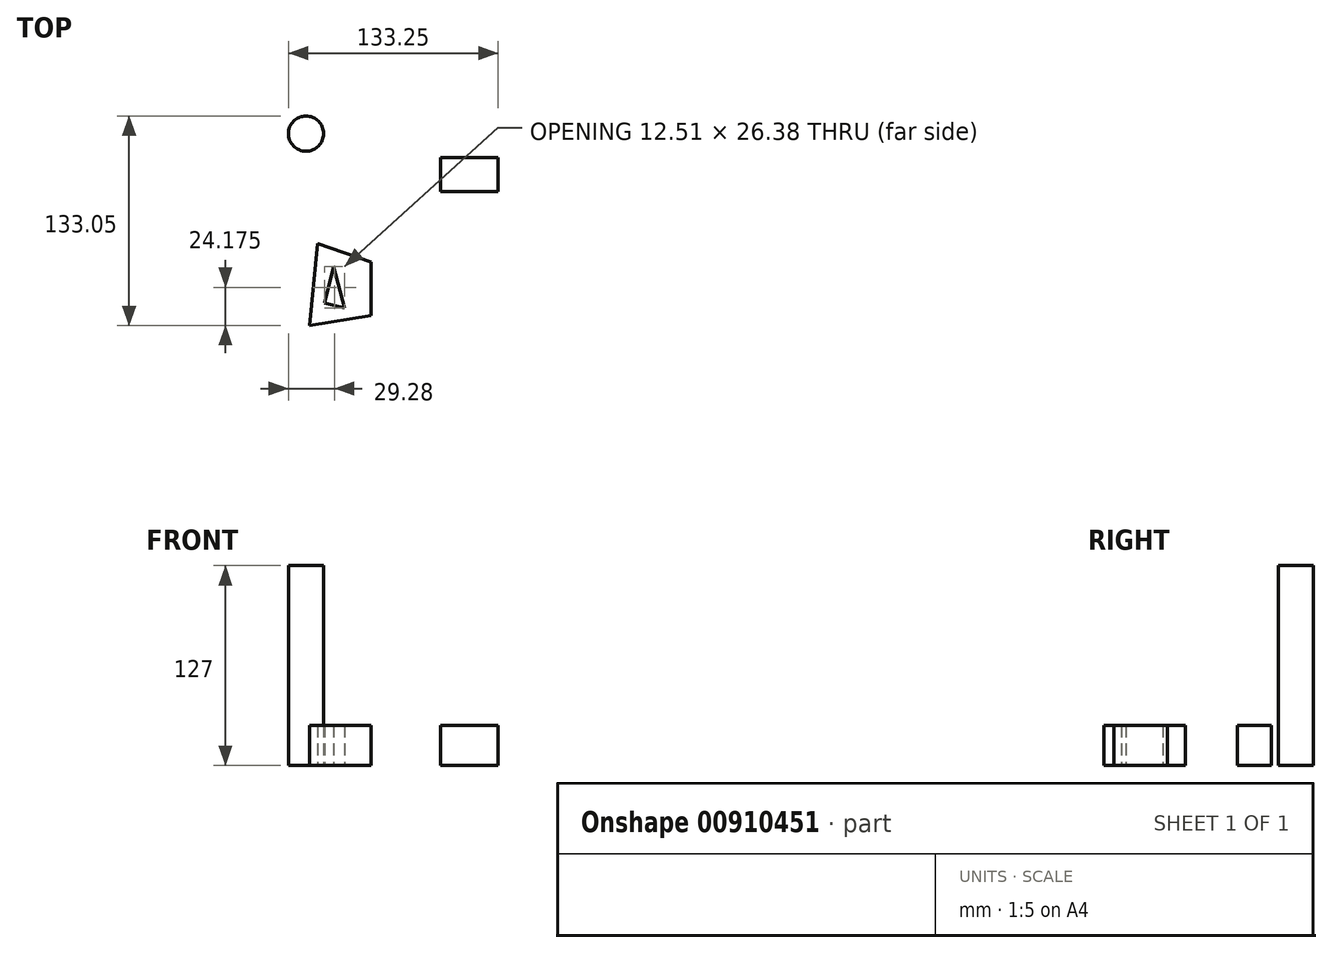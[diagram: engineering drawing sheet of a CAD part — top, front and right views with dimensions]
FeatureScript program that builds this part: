
annotation { "Feature Type Name" : "Feature", "Feature Type Description" : "" }
export const myFeature = defineFeature(function(context is Context, id is Id, definition is map)
    precondition{}
    {
        {
            var Q0;
            Q0=qCreatedBy(makeId("Top.planeOp"),FACE);
            var sketch = newSketch(context, id + "F0", { "sketchPlane" : qUnion([Q0])});
            skCircle(sketch, "E0", {"center": v(-62.28, 52.52) * mm, "radius": 11.18 * mm});
            skLineSegment(sketch, "E1.bottom", {"start": v(23.25, 37.16) * mm, "end": v(59.79, 37.16) * mm});
            skLineSegment(sketch, "E1.top", {"start": v(23.25, 15.57) * mm, "end": v(59.79, 15.57) * mm});
            skLineSegment(sketch, "E1.left", {"start": v(23.25, 37.16) * mm, "end": v(23.25, 15.57) * mm});
            skLineSegment(sketch, "E1.right", {"start": v(59.79, 37.16) * mm, "end": v(59.79, 15.57) * mm});
            skLineSegment(sketch, "E2", {"start": v(-55, -17.45) * mm, "end": v(-20.95, -29.08) * mm});
            skLineSegment(sketch, "E3", {"start": v(-20.95, -29.08) * mm, "end": v(-20.95, -63.13) * mm});
            skLineSegment(sketch, "E4", {"start": v(-20.95, -63.13) * mm, "end": v(-59.98, -69.35) * mm});
            skLineSegment(sketch, "E5", {"start": v(-59.98, -69.35) * mm, "end": v(-55, -17.45) * mm});
            skLineSegment(sketch, "E6", {"start": v(-44.62, -31.99) * mm, "end": v(-50.43, -55.24) * mm});
            skLineSegment(sketch, "E7", {"start": v(-50.43, -55.24) * mm, "end": v(-37.93, -58.36) * mm});
            skLineSegment(sketch, "E8", {"start": v(-37.93, -58.36) * mm, "end": v(-44.62, -31.99) * mm});
            skLineSegment(sketch, "E9", {"start": v(-82.91, 71.7) * mm, "end": v(-82.91, 30.26) * mm, "construction": true});
            skSolve(sketch);
        }
        {
            var Q0;
            Q0=makeQuery(id+"F0.imprint","IMPRINT",FACE,{"disambiguationData":[TD([[makeQuery(id+"F0.imprint","IMPRINT",EDGE,{"derivedFrom":sQuery(id+"F0.wireOp",EDGE,"E2")}),-1.0]])]});
            extrude(context, id + "F1", {"entities" : qUnion([Q0]), "depth" : 25.4 * mm, "offsetDistance" : 25.4 * mm});
        }
        {
            var Q0;
            Q0=makeQuery(id+"F0.imprint","IMPRINT",FACE,{"disambiguationData":[TD([[makeQuery(id+"F0.imprint","IMPRINT",EDGE,{"derivedFrom":sQuery(id+"F0.wireOp",EDGE,"E1.bottom")}),-1.0]])]});
            extrude(context, id + "F2", {"entities" : qUnion([Q0]), "depth" : 25.4 * mm, "offsetDistance" : 25.4 * mm});
        }
        {
            var Q0;
            Q0=makeQuery(id+"F0.imprint","IMPRINT",FACE,{"disambiguationData":[TD([[makeQuery(id+"F0.imprint","IMPRINT",EDGE,{"derivedFrom":sQuery(id+"F0.wireOp",EDGE,"E0")}),1.0]])]});
            extrude(context, id + "F3", {"entities" : qUnion([Q0]), "depth" : 127 * mm, "offsetDistance" : 25.4 * mm});
        }
    });
